# Revit family: CENTUM Doppel-Rollenlager, axial
name_source: partatom
category: HLS-Bauteile
revit_build: Autodesk Revit 2017 (Build: 20190507_1515(x64)
units: mm (PartAtom-declared; Revit-internal decimal feet)

## family parameters
Arbeitsebenenbasiert = Ja
Beim Laden mit Abzugskörper schneiden = Nein
Bemaßung runder Anschluss = Durchmesser verwenden
Gemeinsam genutzt = Ja
Immer vertikal = Nein
Raumberechnungspunkt = Nein
Teiletyp = Normal

## types (36) — shared parameters
Doppel-Rollenlager, axial = MEFA Doppel-Rollenlager , axial  813-1350 DR200 : MEFA Doppel-Rollenlager, axial  813-1350 DR200
Fabrikat = MEFA
Firma = MEFA Befestigungs- und Montagesysteme GmbH
Kurztext1 = Rollenlager doppel axial
Material = Stahl
Materialname = S235
Mengeneinheit = St
Sicherheitsfaktor = 1.54
Vorgabe-Ansicht = 1219 mm
vpe = 1 St

## per-type parameters (varying)
| type | Artikelnummer | Breite mit Laschen | EAN | Gewicht | Gewicht pro Bauteil | Höhe | Kurztext2 | Langloch | Lasttyp | Lochabstand längs | Lochabstand quer | Länge | Oberflaeche | Stärke Material | max. Auflagenbreite | max. zul. Last | min. Auflagenbreite |
| Doppel-Rollenlager, axial  219- 406 DR005, fvz | 150df040406 | 130 mm | 4250928434968 | 4.14 kg | 4.14 kg | 86 mm | 219 - 406 mm 5 kN fsv | 12x24 mm | DR 005 | 110 mm  [stored 0.360892 ft] | 100 mm  [stored 0.328084 ft] | 220 mm  [stored 0.721785 ft] | feuerstückverzinkt | 4 mm  [stored 0.0131234 ft] | 406 mm | 5.00 kN | 219 mm |
| Doppel-Rollenlager, axial  219- 406 DR005, gvz | 150dg040406 | 130 mm | 4250928435095 | 3.99 kg | 3.99 kg | 86 mm | 219 - 406 mm 5 kN gvz | 12x24 mm | DR 005 | 110 mm  [stored 0.360892 ft] | 100 mm  [stored 0.328084 ft] | 220 mm  [stored 0.721785 ft] | galvanisch verzinkt | 4 mm  [stored 0.0131234 ft] | 406 mm | 5.00 kN | 219 mm |
| Doppel-Rollenlager, axial  219- 406 DR005, roh | 150dr040406 | 130 mm | 4250928435224 | 3.99 kg | 3.99 kg | 86 mm | 219 - 406 mm 5 kN roh | 12x24 mm | DR 005 | 110 mm  [stored 0.360892 ft] | 100 mm  [stored 0.328084 ft] | 220 mm  [stored 0.721785 ft] | roh | 4 mm  [stored 0.0131234 ft] | 406 mm | 5.00 kN | 219 mm |
| Doppel-Rollenlager, axial  323- 660 DR015, fvz | 150df050660 | 150 mm | 4250928434975 | 9.44 kg | 9.44 kg | 109 mm | 323 - 660 mm 15 kN fsv | 14x28 mm | DR 015 | 170 mm  [stored 0.557743 ft] | 120 mm  [stored 0.393701 ft] | 335 mm  [stored 1.09908 ft] | feuerstückverzinkt | 6 mm  [stored 0.019685 ft] | 660 mm | 15.00 kN | 323 mm |
| Doppel-Rollenlager, axial  323- 660 DR015, gvz | 150dg050660 | 150 mm | 4250928435101 | 9.20 kg | 9.20 kg | 109 mm | 323 - 660 mm 15 kN gvz | 14x28 mm | DR 015 | 170 mm  [stored 0.557743 ft] | 120 mm  [stored 0.393701 ft] | 335 mm  [stored 1.09908 ft] | galvanisch verzinkt | 6 mm  [stored 0.019685 ft] | 660 mm | 15.00 kN | 323 mm |
| Doppel-Rollenlager, axial  323- 660 DR015, roh | 150dr050660 | 150 mm | 4250928435231 | 9.20 kg | 9.20 kg | 109 mm | 323 - 660 mm 15 kN roh | 14x28 mm | DR 015 | 170 mm  [stored 0.557743 ft] | 120 mm  [stored 0.393701 ft] | 335 mm  [stored 1.09908 ft] | roh | 6 mm  [stored 0.019685 ft] | 660 mm | 15.00 kN | 323 mm |
| Doppel-Rollenlager, axial  323- 660 DR025, fvz | 150df060660 | 150 mm | 4250928434982 | 9.50 kg | 9.50 kg | 109 mm | 323 - 660 mm 25 kN fsv | 14x28 mm | DR 025 | 170 mm  [stored 0.557743 ft] | 120 mm  [stored 0.393701 ft] | 335 mm  [stored 1.09908 ft] | feuerstückverzinkt | 6 mm  [stored 0.019685 ft] | 660 mm | 25.00 kN | 323 mm |
| Doppel-Rollenlager, axial  323- 660 DR025, gvz | 150dg060660 | 150 mm | 4250928435118 | 9.26 kg | 9.26 kg | 109 mm | 323 - 660 mm 25 kN gvz | 14x28 mm | DR 025 | 170 mm  [stored 0.557743 ft] | 120 mm  [stored 0.393701 ft] | 335 mm  [stored 1.09908 ft] | galvanisch verzinkt | 6 mm  [stored 0.019685 ft] | 660 mm | 25.00 kN | 323 mm |
| Doppel-Rollenlager, axial  323- 660 DR025, roh | 150dr060660 | 150 mm | 4250928435248 | 9.26 kg | 9.26 kg | 109 mm | 323 - 660 mm 25 kN roh | 14x28 mm | DR 025 | 170 mm  [stored 0.557743 ft] | 120 mm  [stored 0.393701 ft] | 335 mm  [stored 1.09908 ft] | roh | 6 mm  [stored 0.019685 ft] | 660 mm | 25.00 kN | 323 mm |
| Doppel-Rollenlager, axial  508- 965 DR025, fvz | 150df060965 | 200 mm | 4250928434999 | 21.44 kg | 21.44 kg | 145 mm | 508 - 965 mm 25 kN fsv | 18x36 mm | DR 025 | 250 mm  [stored 0.82021 ft] | 160 mm  [stored 0.524934 ft] | 478 mm  [stored 1.56824 ft] | feuerstückverzinkt | 6 mm  [stored 0.019685 ft] | 965 mm | 25.00 kN | 508 mm |
| Doppel-Rollenlager, axial  508- 965 DR025, gvz | 150dg060965 | 200 mm | 4250928435125 | 20.99 kg | 20.99 kg | 145 mm | 508 - 965 mm 25 kN gvz | 18x36 mm | DR 025 | 250 mm  [stored 0.82021 ft] | 160 mm  [stored 0.524934 ft] | 478 mm  [stored 1.56824 ft] | galvanisch verzinkt | 6 mm  [stored 0.019685 ft] | 965 mm | 25.00 kN | 508 mm |
| Doppel-Rollenlager, axial  508- 965 DR025, roh | 150dr060965 | 200 mm | 4250928435255 | 20.99 kg | 20.99 kg | 145 mm | 508 - 965 mm 25 kN roh | 18x36 mm | DR 025 | 250 mm  [stored 0.82021 ft] | 160 mm  [stored 0.524934 ft] | 478 mm  [stored 1.56824 ft] | roh | 6 mm  [stored 0.019685 ft] | 965 mm | 25.00 kN | 508 mm |
| Doppel-Rollenlager, axial  508- 965 DR050, fvz | 150df080965 | 210 mm | 4250928435002 | 23.38 kg | 23.38 kg | 145 mm | 508 - 965 mm 50 kN fsv | 18x36 mm | DR 050 | 250 mm  [stored 0.82021 ft] | 170 mm  [stored 0.557743 ft] | 478 mm  [stored 1.56824 ft] | feuerstückverzinkt | 8 mm  [stored 0.0262467 ft] | 965 mm | 50.00 kN | 508 mm |
| Doppel-Rollenlager, axial  508- 965 DR050, gvz | 150dg080965 | 210 mm | 4250928435132 | 22.50 kg | 22.50 kg | 145 mm | 508 - 965 mm 50 kN gvz | 18x36 mm | DR 050 | 250 mm  [stored 0.82021 ft] | 170 mm  [stored 0.557743 ft] | 478 mm  [stored 1.56824 ft] | galvanisch verzinkt | 8 mm  [stored 0.0262467 ft] | 965 mm | 50.00 kN | 508 mm |
| Doppel-Rollenlager, axial  508- 965 DR050, roh | 150dr080965 | 210 mm | 4250928435262 | 22.93 kg | 22.93 kg | 145 mm | 508 - 965 mm 50 kN roh | 18x36 mm | DR 050 | 250 mm  [stored 0.82021 ft] | 170 mm  [stored 0.557743 ft] | 478 mm  [stored 1.56824 ft] | roh | 8 mm  [stored 0.0262467 ft] | 965 mm | 50.00 kN | 508 mm |
| Doppel-Rollenlager, axial  508- 965 DR100, fvz | 150df100965 | 220 mm | 4250928435026 | 25.24 kg | 25.24 kg | 145 mm | 508 - 965 mm 100 kN fsv | 18x36 mm | DR 100 | 250 mm  [stored 0.82021 ft] | 180 mm  [stored 0.590551 ft] | 478 mm  [stored 1.56824 ft] | feuerstückverzinkt | 10 mm  [stored 0.0328084 ft] | 965 mm | 100.00 kN | 508 mm |
| Doppel-Rollenlager, axial  508- 965 DR100, gvz | 150dg100965 | 220 mm | 4250928435156 | 24.30 kg | 24.30 kg | 145 mm | 508 - 965 mm 100 kN gvz | 18x36 mm | DR 100 | 250 mm  [stored 0.82021 ft] | 180 mm  [stored 0.590551 ft] | 478 mm  [stored 1.56824 ft] | galvanisch verzinkt | 10 mm  [stored 0.0328084 ft] | 965 mm | 100.00 kN | 508 mm |
| Doppel-Rollenlager, axial  508- 965 DR100, roh | 150dr100965 | 220 mm | 4250928435286 | 24.77 kg | 24.77 kg | 145 mm | 508 - 965 mm 100 kN roh | 18x36 mm | DR 100 | 250 mm  [stored 0.82021 ft] | 180 mm  [stored 0.590551 ft] | 478 mm  [stored 1.56824 ft] | roh | 10 mm  [stored 0.0328084 ft] | 965 mm | 100.00 kN | 508 mm |
| Doppel-Rollenlager, axial  813-1350 DR050, fvz | 150df081350 | 258 mm | 4250928435019 | 56.49 kg | 56.49 kg | 195 mm | 813 - 1.350 mm 50 kN fsv | 23x46 mm | DR 050 | 360 mm  [stored 1.1811 ft] | 208 mm | 652 mm  [stored 2.13911 ft] | feuerstückverzinkt | 8 mm  [stored 0.0262467 ft] | 1.350 mm | 50.00 kN | 813 mm |
| Doppel-Rollenlager, axial  813-1350 DR050, gvz | 150dg081350 | 258 mm | 4250928435149 | 54.70 kg | 54.70 kg | 195 mm | 813 - 1.350 mm 50 kN gvz | 23x46 mm | DR 050 | 360 mm  [stored 1.1811 ft] | 208 mm | 652 mm  [stored 2.13911 ft] | galvanisch verzinkt | 8 mm  [stored 0.0262467 ft] | 1.350 mm | 50.00 kN | 813 mm |
| Doppel-Rollenlager, axial  813-1350 DR050, roh | 150dr081350 | 258 mm | 4250928435279 | 55.63 kg | 55.63 kg | 195 mm | 813 - 1.350 mm 50 kN roh | 23x46 mm | DR 050 | 360 mm  [stored 1.1811 ft] | 208 mm | 652 mm  [stored 2.13911 ft] | roh | 8 mm  [stored 0.0262467 ft] | 1.350 mm | 50.00 kN | 813 mm |
| Doppel-Rollenlager, axial  819-1350 DR100, fvz | 150df101350 | 268 mm | 4250928435033 | 60.16 kg | 60.16 kg | 195 mm | 813 - 1.350 mm 100 kN fsv | 23x46 mm | DR 100 | 360 mm  [stored 1.1811 ft] | 218 mm  [stored 0.715223 ft] | 652 mm  [stored 2.13911 ft] | feuerstückverzinkt | 10 mm  [stored 0.0328084 ft] | 1.350 mm | 100.00 kN | 813 mm |
| Doppel-Rollenlager, axial  819-1350 DR100, gvz | 150dg101350 | 268 mm | 4250928435163 | 59.20 kg | 59.20 kg | 195 mm | 813 - 1.350 mm 100 kN gvz | 23x46 mm | DR 100 | 360 mm  [stored 1.1811 ft] | 218 mm  [stored 0.715223 ft] | 652 mm  [stored 2.13911 ft] | galvanisch verzinkt | 10 mm  [stored 0.0328084 ft] | 1.350 mm | 100.00 kN | 813 mm |
| Doppel-Rollenlager, axial  813-1350 DR100, roh | 150dr101350 | 268 mm | 4250928435293 | 59.29 kg | 59.29 kg | 195 mm | 813 - 1.350 mm 100 kN roh | 23x46 mm | DR 100 | 360 mm  [stored 1.1811 ft] | 218 mm  [stored 0.715223 ft] | 652 mm  [stored 2.13911 ft] | roh | 10 mm  [stored 0.0328084 ft] | 1.350 mm | 100.00 kN | 813 mm |
| Doppel-Rollenlager, axial  813-1350 DR200, fvz | 150df121350 | 278 mm | 4250928435057 | 63.40 kg | 63.40 kg | 195 mm | 813 - 1.350 mm 200 kN fsv | 23x46 mm | DR 200 | 360 mm  [stored 1.1811 ft] | 228 mm  [stored 0.748031 ft] | 652 mm  [stored 2.13911 ft] | feuerstückverzinkt | 12 mm  [stored 0.0393701 ft] | 1.350 mm | 200.00 kN | 813 mm |
| Doppel-Rollenlager, axial  813-1350 DR200, gvz | 150dg121350 | 278 mm | 4250928435187 | 61.30 kg | 61.30 kg | 195 mm | 813 - 1.350 mm 200 kN gvz | 23x46 mm | DR 200 | 360 mm  [stored 1.1811 ft] | 228 mm  [stored 0.748031 ft] | 652 mm  [stored 2.13911 ft] | galvanisch verzinkt | 12 mm  [stored 0.0393701 ft] | 1.350 mm | 200.00 kN | 813 mm |
| Doppel-Rollenlager, axial  813-1350 DR200, roh | 150dr121350 | 278 mm | 4250928435316 | 62.54 kg | 62.54 kg | 195 mm | 813 - 1.350 mm 200 kN roh | 23x46 mm | DR 200 | 360 mm  [stored 1.1811 ft] | 228 mm  [stored 0.748031 ft] | 652 mm  [stored 2.13911 ft] | roh | 12 mm  [stored 0.0393701 ft] | 1.350 mm | 200.00 kN | 813 mm |
| Doppel-Rollenlager, axial 1120-1920 DR100, fvz | 150df101920 | 330 mm | 4250928435040 | 112.88 kg | 112.88 kg | 274 mm | 1120 - 1.920 mm 100 kN fsv | 27x54 mm | DR 100 | 500 mm  [stored 1.64042 ft] | 270 mm  [stored 0.885827 ft] | 870 mm  [stored 2.85433 ft] | feuerstückverzinkt | 10 mm  [stored 0.0328084 ft] | 1.920 mm | 100.00 kN | 1.120 mm |
| Doppel-Rollenlager, axial 1120-1920 DR100, gvz | 150dg101920 | 330 mm | 4250928435170 | 109.30 kg | 109.30 kg | 274 mm | 1120 - 1.920 mm 100 kN gvz | 27x54 mm | DR 100 | 500 mm  [stored 1.64042 ft] | 270 mm  [stored 0.885827 ft] | 870 mm  [stored 2.85433 ft] | galvanisch verzinkt | 10 mm  [stored 0.0328084 ft] | 1.920 mm | 100.00 kN | 1.120 mm |
| Doppel-Rollenlager, axial 1120-1920 DR100, roh | 150dr101920 | 330 mm | 4250928435309 | 111.38 kg | 111.38 kg | 274 mm | 1120 - 1.920 mm 100 kN roh | 27x54 mm | DR 100 | 500 mm  [stored 1.64042 ft] | 270 mm  [stored 0.885827 ft] | 870 mm  [stored 2.85433 ft] | roh | 10 mm  [stored 0.0328084 ft] | 1.920 mm | 100.00 kN | 1.120 mm |
| Doppel-Rollenlager, axial 1120-1920 DR200, fvz | 150df121920 | 340 mm | 4250928435064 | 118.96 kg | 118.96 kg | 274 mm | 1120 - 1.920 mm 200 kN fsv | 27x54 mm | DR 200 | 500 mm  [stored 1.64042 ft] | 280 mm  [stored 0.918635 ft] | 870 mm  [stored 2.85433 ft] | feuerstückverzinkt | 12 mm  [stored 0.0393701 ft] | 1.920 mm | 200.00 kN | 1.120 mm |
| Doppel-Rollenlager, axial 1120-1920 DR200, gvz | 150dg121920 | 340 mm | 4250928435194 | 115.10 kg | 115.10 kg | 274 mm | 1120 - 1.920 mm 200 kN gvz | 27x54 mm | DR 200 | 500 mm  [stored 1.64042 ft] | 280 mm  [stored 0.918635 ft] | 870 mm  [stored 2.85433 ft] | galvanisch verzinkt | 12 mm  [stored 0.0393701 ft] | 1.920 mm | 200.00 kN | 1.120 mm |
| Doppel-Rollenlager, axial 1120-1920 DR200, roh | 150dr121920 | 340 mm | 4250928435323 | 117.45 kg | 117.45 kg | 274 mm | 1120 - 1.920 mm 200 kN roh | 27x54 mm | DR 200 | 500 mm  [stored 1.64042 ft] | 280 mm  [stored 0.918635 ft] | 870 mm  [stored 2.85433 ft] | roh | 12 mm  [stored 0.0393701 ft] | 1.920 mm | 200.00 kN | 1.120 mm |
| Doppel-Rollenlager, axial 1120-1920 DR300, fvz | 150df151920 | 350 mm | 4250928435071 | 128.51 kg | 128.51 kg | 274 mm | 1120 - 1.920 mm 300 kN fsv | 27x54 mm | DR 300 | 500 mm  [stored 1.64042 ft] | 290 mm  [stored 0.951444 ft] | 870 mm  [stored 2.85433 ft] | feuerstückverzinkt | 15 mm  [stored 0.0492126 ft] | 1.920 mm | 300.00 kN | 1.120 mm |
| Doppel-Rollenlager, axial 1120-1920 DR300, gvz | 150dg151920 | 350 mm | 4250928435200 | 124.20 kg | 124.20 kg | 274 mm | 1120 - 1.920 mm 300 kN gvz | 27x54 mm | DR 300 | 500 mm  [stored 1.64042 ft] | 290 mm  [stored 0.951444 ft] | 870 mm  [stored 2.85433 ft] | galvanisch verzinkt | 15 mm  [stored 0.0492126 ft] | 1.920 mm | 300.00 kN | 1.120 mm |
| Doppel-Rollenlager, axial 1120-1920 DR300, roh | 150dr151920 | 350 mm | 4250928435330 | 126.98 kg | 126.98 kg | 274 mm | 1120 - 1.920 mm 300 kN roh | 27x54 mm | DR 300 | 500 mm  [stored 1.64042 ft] | 290 mm  [stored 0.951444 ft] | 870 mm  [stored 2.85433 ft] | roh | 15 mm  [stored 0.0492126 ft] | 1.920 mm | 300.00 kN | 1.120 mm |

note: [stored X ft] marks values corroborated as IEEE doubles in the binary element streams (Revit-internal decimal feet)
